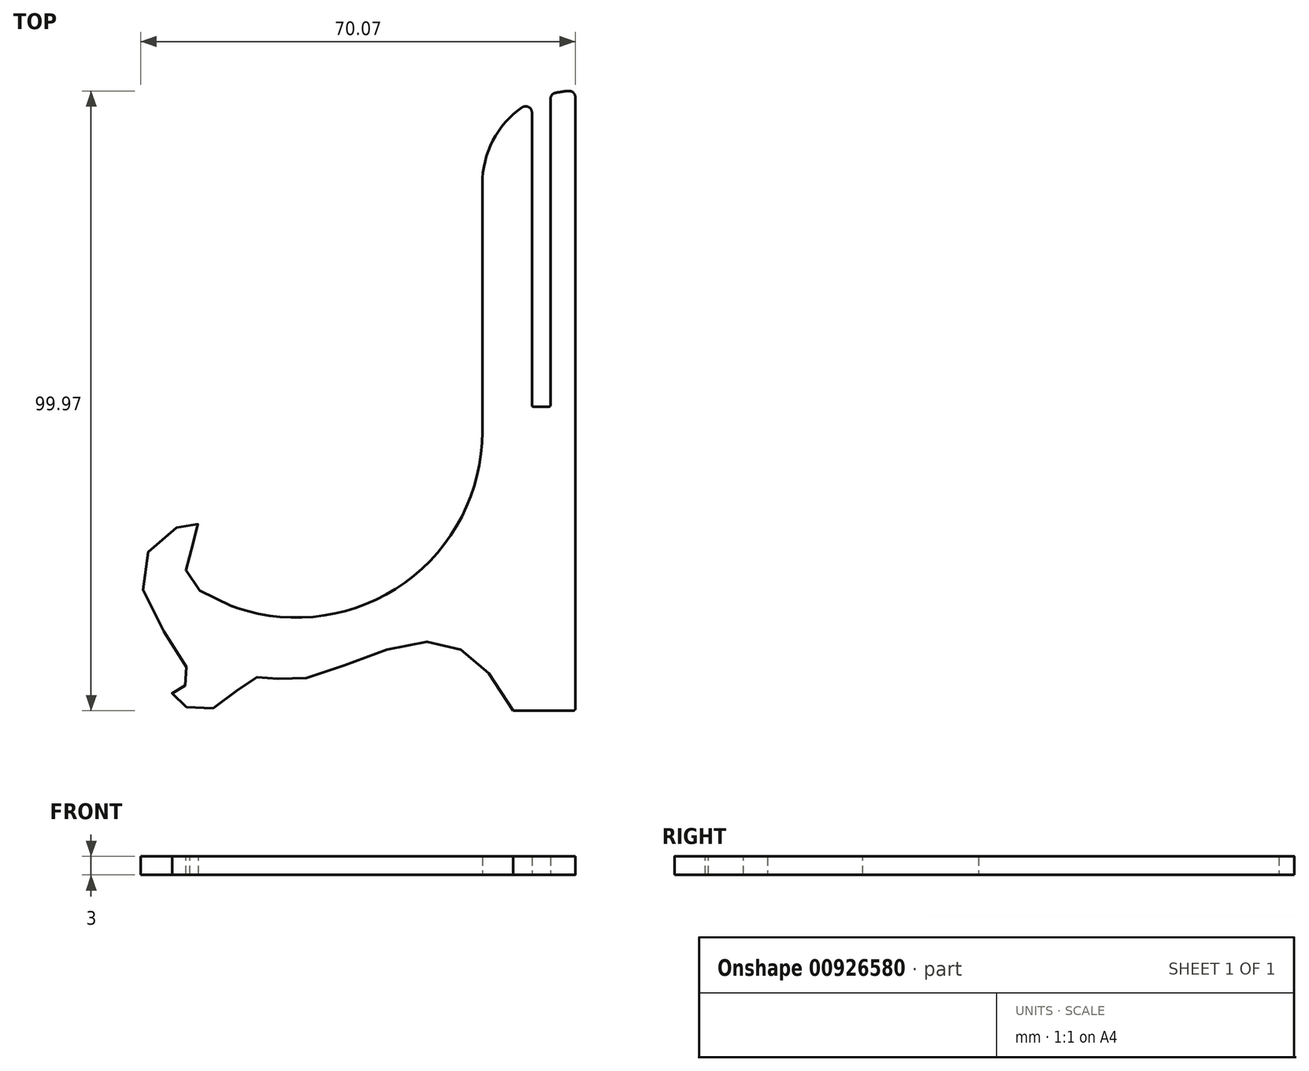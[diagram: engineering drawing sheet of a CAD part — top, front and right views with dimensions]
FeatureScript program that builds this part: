
annotation { "Feature Type Name" : "Feature", "Feature Type Description" : "" }
export const myFeature = defineFeature(function(context is Context, id is Id, definition is map)
    precondition{}
    {
        {
            var Q0;
            Q0=qCreatedBy(makeId("Top.planeOp"),FACE);
            var sketch = newSketch(context, id + "F0", { "sketchPlane" : qUnion([Q0])});
            skLineSegment(sketch, "E0", {"start": v(0, 0.3) * mm, "end": v(0, 98.96) * mm});
            skLineSegment(sketch, "E1", {"start": v(-15, 85) * mm, "end": v(-15, 45) * mm});
            skLineSegment(sketch, "E2", {"start": v(-4, 98.67) * mm, "end": v(-4, 49.3) * mm});
            skLineSegment(sketch, "E3", {"start": v(-7, 96.49) * mm, "end": v(-7, 49.3) * mm});
            skLineSegment(sketch, "E4.trimOffspring", {"start": v(-6.7, 49) * mm, "end": v(-4.3, 49) * mm});
            skArc(sketch, "E5", {"start": v(-55.48, 16.89) * mm, "mid": v(-27.89, 20.36) * mm, "end": v(-15, 45) * mm});
            skLineSegment(sketch, "E6", {"start": v(-0.3, 0) * mm, "end": v(-10, 0) * mm});
            skFitSpline(sketch, "E7", {"points": [v(-10, 0) * mm, v(-23.84, 11.12) * mm, v(-45, 5) * mm, v(-51.95, 5.2) * mm, v(-60, 0) * mm, v(-65, 2.96) * mm, v(-62.2, 4.82) * mm, v(-70, 22.85) * mm, v(-60.94, 30.16) * mm, v(-62.8, 23.33) * mm, v(-54.58, 16.57) * mm], "startDerivative": vector(-87.8, 161.53) * mm, "endDerivative": vector(149.44, -51.66) * mm});
            skPoint(sketch, "E8.trimOffspring.end.orphan", {"position": v(-15, 0) * mm});
            skArc(sketch, "E9", {"start": v(-1.07, 99.96) * mm, "mid": v(-2.15, 99.85) * mm, "end": v(-3.21, 99.65) * mm});
            skPoint(sketch, "E10.orphan", {"position": v(0, 112.49) * mm});
            skArc(sketch, "E11.trimOffspring", {"start": v(-8.57, 97.3) * mm, "mid": v(-13.3, 91.94) * mm, "end": v(-15, 85) * mm});
            skPoint(sketch, "E12.visualSharp", {"position": v(-7, 98.27) * mm});
            skArc(sketch, "E12.filletArc", {"start": v(-7, 96.49) * mm, "mid": v(-7.54, 97.38) * mm, "end": v(-8.57, 97.3) * mm});
            skPoint(sketch, "E13.visualSharp", {"position": v(-4, 99.46) * mm});
            skArc(sketch, "E13.filletArc", {"start": v(-3.21, 99.65) * mm, "mid": v(-3.78, 99.3) * mm, "end": v(-4, 98.67) * mm});
            skPoint(sketch, "E14.visualSharp", {"position": v(0, 100) * mm});
            skArc(sketch, "E14.filletArc", {"start": v(0, 98.96) * mm, "mid": v(-0.32, 99.7) * mm, "end": v(-1.07, 99.96) * mm});
            skPoint(sketch, "E15.visualSharp", {"position": v(-7, 49) * mm});
            skArc(sketch, "E15.filletArc", {"start": v(-7, 49.3) * mm, "mid": v(-6.91, 49.09) * mm, "end": v(-6.7, 49) * mm});
            skPoint(sketch, "E16.visualSharp", {"position": v(-4, 49) * mm});
            skArc(sketch, "E16.filletArc", {"start": v(-4.3, 49) * mm, "mid": v(-4.09, 49.09) * mm, "end": v(-4, 49.3) * mm});
            skPoint(sketch, "E17.visualSharp", {"position": v(0, 0) * mm});
            skArc(sketch, "E17.filletArc", {"start": v(-0.3, 0) * mm, "mid": v(-0.09, 0.09) * mm, "end": v(0, 0.3) * mm});
            skSolve(sketch);
        }
        {
            var Q0;
            Q0 = qSketchRegion(id + "F0", true);
            extrude(context, id + "F1", {"entities" : qUnion([Q0]), "depth" : 3 * mm, "offsetDistance" : 25 * mm});
        }
    });
